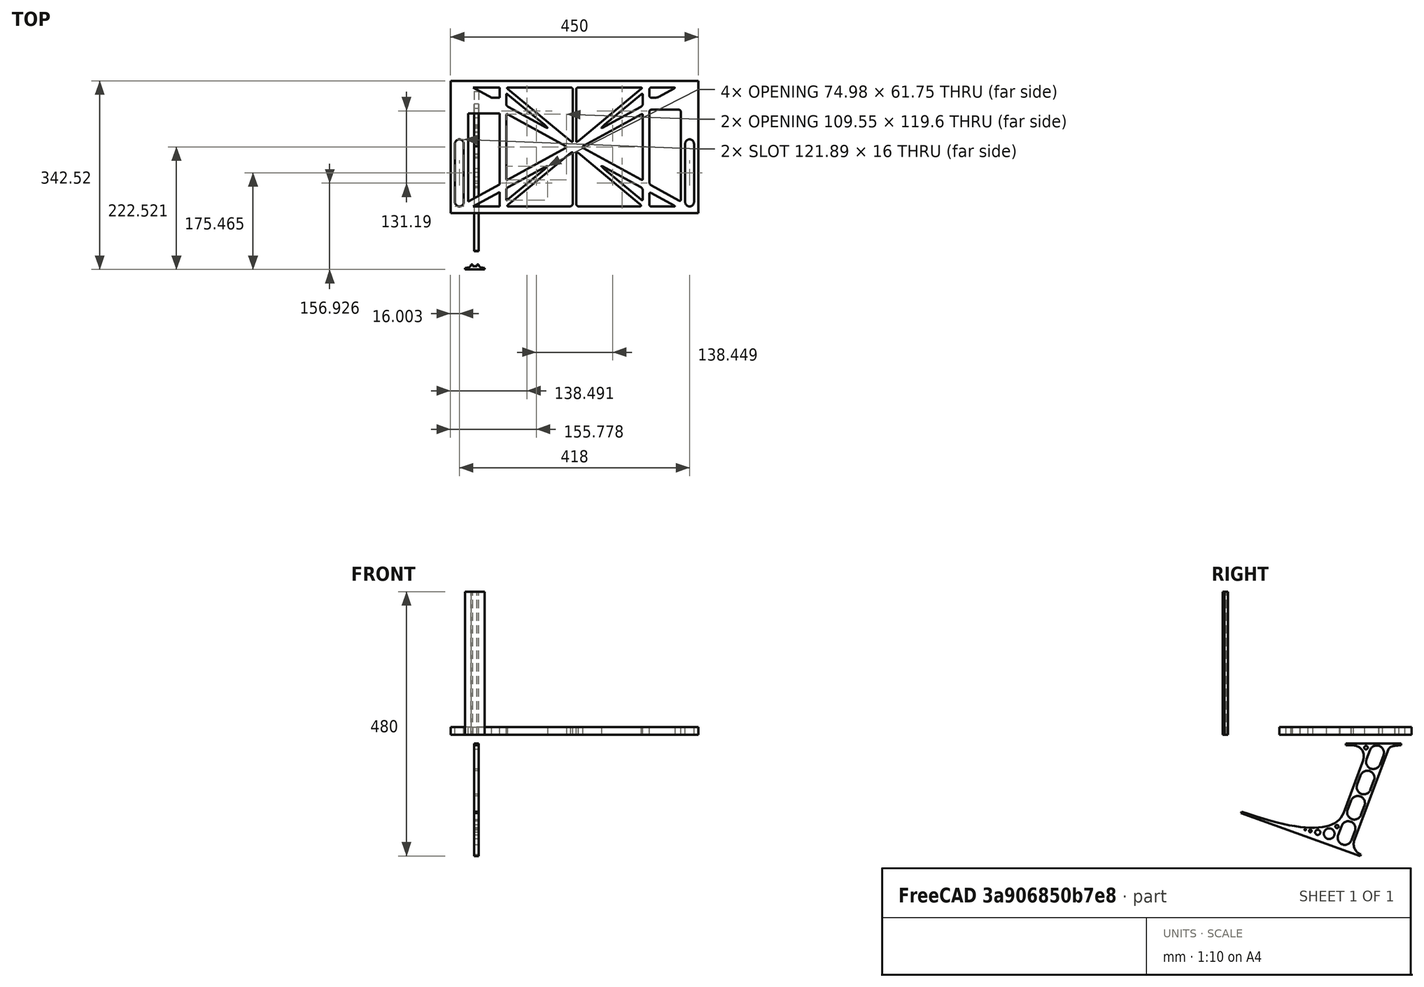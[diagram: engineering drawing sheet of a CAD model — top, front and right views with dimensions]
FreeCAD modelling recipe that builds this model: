
FCSTD DOCUMENT  (FreeCAD 0.19R0.19.2)
Label: laptopStand1156FCStd
License: All rights reserved
LicenseURL: http://en.wikipedia.org/wiki/All_rights_reserved
objects: Sketcher::SketchObject×3, Part::Extrusion×3
note: 6 computed .brp shape members not serialized (recipe doc carries the construction recipe); baked Part::Feature solids carry a one-line shape summary decoded from their .brp

FEATURE [Sketcher::SketchObject] Sketch
  FullyConstrained = true
  sketch-geometry (318):
    g0: LineSegment StartX=-10.9272 StartY=-82.7794 StartZ=0 EndX=46.0728 EndY=-51.4823 EndZ=0
    g1: LineSegment StartX=-10.9272 StartY=77.3346 StartZ=0 EndX=-10.9272 EndY=-82.7794 EndZ=0
    g2: LineSegment StartX=-1.92719 StartY=-91.7794 StartZ=0 EndX=46.0728 EndY=-91.7794 EndZ=0
    g3: LineSegment StartX=46.0728 StartY=-65.424 StartZ=0 EndX=-1.92719 EndY=-91.7794 EndZ=0
    g4: LineSegment StartX=46.0728 StartY=-65.424 StartZ=0 EndX=46.0728 EndY=-91.7794 EndZ=0
    g5: LineSegment StartX=46.0728 StartY=77.3346 StartZ=0 EndX=46.0728 EndY=-51.4823 EndZ=0
    g6: LineSegment StartX=-42.9272 StartY=136.221 StartZ=0 EndX=-42.9272 EndY=-103.779 EndZ=0
    g7: LineSegment StartX=407.073 StartY=136.221 StartZ=0 EndX=407.073 EndY=-103.779 EndZ=0
    g8: ArcOfCircle CenterX=-26.9272 CenterY=22.1087 CenterZ=0 NormalX=0 NormalY=0 NormalZ=1 AngleXU=0 Radius=8 StartAngle=1e-16 EndAngle=3.14159
    g9: ArcOfCircle CenterX=-26.9272 CenterY=-83.7794 CenterZ=0 NormalX=0 NormalY=0 NormalZ=1 AngleXU=0 Radius=8 StartAngle=3.14159 EndAngle=6.28319
    g10: LineSegment StartX=-34.9272 StartY=22.1087 StartZ=0 EndX=-34.9272 EndY=-83.7794 EndZ=0
    g11: LineSegment StartX=-18.9272 StartY=22.1087 StartZ=0 EndX=-18.9272 EndY=-83.7794 EndZ=0
    g12: ArcOfCircle CenterX=391.073 CenterY=22.1087 CenterZ=0 NormalX=0 NormalY=0 NormalZ=1 AngleXU=0 Radius=8 StartAngle=-4.4e-15 EndAngle=3.14159
    g13: LineSegment StartX=399.073 StartY=22.1087 StartZ=0 EndX=399.073 EndY=-83.7794 EndZ=0
    g14: LineSegment StartX=383.073 StartY=22.1087 StartZ=0 EndX=383.073 EndY=-83.7794 EndZ=0
    g15: ArcOfCircle CenterX=391.073 CenterY=-83.7794 CenterZ=0 NormalX=0 NormalY=0 NormalZ=1 AngleXU=0 Radius=8 StartAngle=3.14159 EndAngle=6.28319
    g16: Circle CenterX=175.022 CenterY=27.0628 CenterZ=0 NormalX=0 NormalY=0 NormalZ=1 AngleXU=0 Radius=1
    g17: Circle CenterX=179.022 CenterY=24.8665 CenterZ=0 NormalX=0 NormalY=0 NormalZ=1 AngleXU=0 Radius=1
    g18: Circle CenterX=179.022 CenterY=27.0628 CenterZ=0 NormalX=0 NormalY=0 NormalZ=1 AngleXU=0 Radius=1
    g19: BSplineCurve PolesCount=3 KnotsCount=2 Degree=2 IsPeriodic=0
    g20: GeomPoint X=175.022 Y=27.0628 Z=0
    g21: GeomPoint X=179.022 Y=27.0628 Z=0
    g22: Circle CenterX=189.124 CenterY=27.0628 CenterZ=0 NormalX=0 NormalY=0 NormalZ=1 AngleXU=0 Radius=1
    g23: Circle CenterX=185.124 CenterY=24.8665 CenterZ=0 NormalX=0 NormalY=0 NormalZ=1 AngleXU=0 Radius=1
    g24: Circle CenterX=185.124 CenterY=27.0628 CenterZ=0 NormalX=0 NormalY=0 NormalZ=1 AngleXU=0 Radius=1
    g25: BSplineCurve PolesCount=3 KnotsCount=2 Degree=2 IsPeriodic=0
    g26: GeomPoint X=189.124 Y=27.0628 Z=0
    g27: GeomPoint X=185.124 Y=27.0628 Z=0
    g28: Circle CenterX=175.022 CenterY=5.37834 CenterZ=0 NormalX=0 NormalY=0 NormalZ=1 AngleXU=0 Radius=1
    g29: Circle CenterX=179.022 CenterY=7.57463 CenterZ=0 NormalX=0 NormalY=0 NormalZ=1 AngleXU=0 Radius=1
    g30: Circle CenterX=179.022 CenterY=5.34704 CenterZ=0 NormalX=0 NormalY=0 NormalZ=1 AngleXU=0 Radius=1
    g31: BSplineCurve PolesCount=3 KnotsCount=2 Degree=2 IsPeriodic=0
    g32: GeomPoint X=175.022 Y=5.37834 Z=0
    g33: GeomPoint X=179.022 Y=5.34704 Z=0
    g34: Circle CenterX=189.124 CenterY=5.37834 CenterZ=0 NormalX=0 NormalY=0 NormalZ=1 AngleXU=0 Radius=1
    g35: Circle CenterX=185.124 CenterY=7.57463 CenterZ=0 NormalX=0 NormalY=0 NormalZ=1 AngleXU=0 Radius=1
    g36: Circle CenterX=185.124 CenterY=5.34704 CenterZ=0 NormalX=0 NormalY=0 NormalZ=1 AngleXU=0 Radius=1
    g37: BSplineCurve PolesCount=3 KnotsCount=2 Degree=2 IsPeriodic=0
    g38: GeomPoint X=189.124 Y=5.37834 Z=0
    g39: GeomPoint X=185.124 Y=5.34704 Z=0
    g40: Circle CenterX=165.871 CenterY=18.1458 CenterZ=0 NormalX=0 NormalY=0 NormalZ=1 AngleXU=0 Radius=1
    g41: Circle CenterX=169.377 CenterY=16.2206 CenterZ=0 NormalX=0 NormalY=0 NormalZ=1 AngleXU=0 Radius=1
    g42: Circle CenterX=165.871 CenterY=14.2954 CenterZ=0 NormalX=0 NormalY=0 NormalZ=1 AngleXU=0 Radius=1
    g43: BSplineCurve PolesCount=3 KnotsCount=2 Degree=2 IsPeriodic=0
    g44: GeomPoint X=165.871 Y=18.1458 Z=0
    g45: GeomPoint X=165.871 Y=14.2954 Z=0
    g46: Circle CenterX=198.275 CenterY=18.1458 CenterZ=0 NormalX=0 NormalY=0 NormalZ=1 AngleXU=0 Radius=1
    g47: Circle CenterX=194.768 CenterY=16.2206 CenterZ=0 NormalX=0 NormalY=0 NormalZ=1 AngleXU=0 Radius=1
    g48: Circle CenterX=198.275 CenterY=14.2954 CenterZ=0 NormalX=0 NormalY=0 NormalZ=1 AngleXU=0 Radius=1
    g49: BSplineCurve PolesCount=3 KnotsCount=2 Degree=2 IsPeriodic=0
    g50: GeomPoint X=198.275 Y=18.1458 Z=0
    g51: GeomPoint X=198.275 Y=14.2954 Z=0
    g52: LineSegment StartX=407.073 StartY=-103.779 StartZ=0 EndX=-42.9272 EndY=-103.779 EndZ=0
    g53: LineSegment StartX=407.073 StartY=136.221 StartZ=0 EndX=-42.9272 EndY=136.221 EndZ=0
    g54: LineSegment StartX=46.0728 StartY=77.3346 StartZ=0 EndX=-10.9272 EndY=77.3346 EndZ=0
    g55: LineSegment StartX=46.0728 StartY=105.865 StartZ=0 EndX=31.5028 EndY=105.865 EndZ=0
    g56: LineSegment StartX=46.0728 StartY=124.221 StartZ=0 EndX=46.0728 EndY=105.865 EndZ=0
    g57: LineSegment StartX=-1.92719 StartY=124.221 StartZ=0 EndX=31.5028 EndY=105.865 EndZ=0
    g58: LineSegment StartX=46.0728 StartY=124.221 StartZ=0 EndX=-1.92719 EndY=124.221 EndZ=0
    g59: Circle CenterX=125.607 CenterY=54.1951 CenterZ=0 NormalX=0 NormalY=0 NormalZ=1 AngleXU=0 Radius=1
    g60: Circle CenterX=139.632 CenterY=46.4944 CenterZ=0 NormalX=0 NormalY=0 NormalZ=1 AngleXU=0 Radius=1
    g61: Circle CenterX=127.326 CenterY=56.7187 CenterZ=0 NormalX=0 NormalY=0 NormalZ=1 AngleXU=0 Radius=1
    g62: BSplineCurve PolesCount=3 KnotsCount=2 Degree=2 IsPeriodic=0
    g63: GeomPoint X=125.607 Y=54.1951 Z=0
    g64: GeomPoint X=127.326 Y=56.7187 Z=0
    g65: Circle CenterX=236.821 CenterY=56.7187 CenterZ=0 NormalX=0 NormalY=0 NormalZ=1 AngleXU=0 Radius=1
    g66: Circle CenterX=224.513 CenterY=46.4944 CenterZ=0 NormalX=0 NormalY=0 NormalZ=1 AngleXU=0 Radius=1
    g67: Circle CenterX=238.538 CenterY=54.1951 CenterZ=0 NormalX=0 NormalY=0 NormalZ=1 AngleXU=0 Radius=1
    g68: BSplineCurve PolesCount=3 KnotsCount=2 Degree=2 IsPeriodic=0
    g69: GeomPoint X=236.821 Y=56.7187 Z=0
    g70: GeomPoint X=238.538 Y=54.1951 Z=0
    g71: Circle CenterX=238.538 CenterY=-21.7539 CenterZ=0 NormalX=0 NormalY=0 NormalZ=1 AngleXU=0 Radius=1
    g72: Circle CenterX=224.513 CenterY=-14.0532 CenterZ=0 NormalX=0 NormalY=0 NormalZ=1 AngleXU=0 Radius=1
    g73: Circle CenterX=236.821 CenterY=-24.2775 CenterZ=0 NormalX=0 NormalY=0 NormalZ=1 AngleXU=0 Radius=1
    g74: BSplineCurve PolesCount=3 KnotsCount=2 Degree=2 IsPeriodic=0
    g75: GeomPoint X=238.538 Y=-21.7539 Z=0
    g76: GeomPoint X=236.821 Y=-24.2775 Z=0
    g77: Circle CenterX=125.607 CenterY=-21.7539 CenterZ=0 NormalX=0 NormalY=0 NormalZ=1 AngleXU=0 Radius=1
    g78: Circle CenterX=139.632 CenterY=-14.0532 CenterZ=0 NormalX=0 NormalY=0 NormalZ=1 AngleXU=0 Radius=1
    g79: Circle CenterX=127.325 CenterY=-24.2775 CenterZ=0 NormalX=0 NormalY=0 NormalZ=1 AngleXU=0 Radius=1
    g80: BSplineCurve PolesCount=3 KnotsCount=2 Degree=2 IsPeriodic=0
    g81: GeomPoint X=125.607 Y=-21.7539 Z=0
    g82: GeomPoint X=127.325 Y=-24.2775 Z=0
    g83: Circle CenterX=302.996 CenterY=111.695 CenterZ=0 NormalX=0 NormalY=0 NormalZ=1 AngleXU=0 Radius=1
    g84: Circle CenterX=306.073 CenterY=114.251 CenterZ=0 NormalX=0 NormalY=0 NormalZ=1 AngleXU=0 Radius=1
    g85: Circle CenterX=306.073 CenterY=110.251 CenterZ=0 NormalX=0 NormalY=0 NormalZ=1 AngleXU=0 Radius=1
    g86: BSplineCurve PolesCount=3 KnotsCount=2 Degree=2 IsPeriodic=0
    g87: GeomPoint X=302.996 Y=111.695 Z=0
    g88: GeomPoint X=306.073 Y=110.251 Z=0
    g89: Circle CenterX=306.073 CenterY=95.2763 CenterZ=0 NormalX=0 NormalY=0 NormalZ=1 AngleXU=0 Radius=1
    g90: Circle CenterX=306.073 CenterY=91.2763 CenterZ=0 NormalX=0 NormalY=0 NormalZ=1 AngleXU=0 Radius=1
    g91: Circle CenterX=302.567 CenterY=89.3511 CenterZ=0 NormalX=0 NormalY=0 NormalZ=1 AngleXU=0 Radius=1
    g92: BSplineCurve PolesCount=3 KnotsCount=2 Degree=2 IsPeriodic=0
    g93: GeomPoint X=306.073 Y=95.2763 Z=0
    g94: GeomPoint X=302.567 Y=89.3511 Z=0
    g95: LineSegment StartX=306.073 StartY=110.251 StartZ=0 EndX=306.073 EndY=95.2763 EndZ=0
    g96: LineSegment StartX=302.996 StartY=111.695 StartZ=0 EndX=236.821 EndY=56.7187 EndZ=0
    g97: LineSegment StartX=238.538 StartY=54.1951 StartZ=0 EndX=302.567 EndY=89.3511 EndZ=0
    g98: Circle CenterX=61.1496 CenterY=111.695 CenterZ=0 NormalX=0 NormalY=0 NormalZ=1 AngleXU=0 Radius=1
    g99: Circle CenterX=58.0728 CenterY=114.251 CenterZ=0 NormalX=0 NormalY=0 NormalZ=1 AngleXU=0 Radius=1
    g100: Circle CenterX=58.0728 CenterY=110.251 CenterZ=0 NormalX=0 NormalY=0 NormalZ=1 AngleXU=0 Radius=1
    g101: BSplineCurve PolesCount=3 KnotsCount=2 Degree=2 IsPeriodic=0
    g102: GeomPoint X=61.1496 Y=111.695 Z=0
    g103: GeomPoint X=58.0728 Y=110.251 Z=0
    g104: Circle CenterX=61.5791 CenterY=89.3511 CenterZ=0 NormalX=0 NormalY=0 NormalZ=1 AngleXU=0 Radius=1
    g105: Circle CenterX=58.0728 CenterY=91.2763 CenterZ=0 NormalX=0 NormalY=0 NormalZ=1 AngleXU=0 Radius=1
    g106: Circle CenterX=58.0728 CenterY=95.2763 CenterZ=0 NormalX=0 NormalY=0 NormalZ=1 AngleXU=0 Radius=1
    g107: BSplineCurve PolesCount=3 KnotsCount=2 Degree=2 IsPeriodic=0
    g108: GeomPoint X=61.5791 Y=89.3511 Z=0
    g109: GeomPoint X=58.0728 Y=95.2763 Z=0
    g110: LineSegment StartX=58.0728 StartY=110.251 StartZ=0 EndX=58.0728 EndY=95.2763 EndZ=0
    g111: LineSegment StartX=61.1496 StartY=111.695 StartZ=0 EndX=127.326 EndY=56.7187 EndZ=0
    g112: LineSegment StartX=125.607 StartY=54.1951 StartZ=0 EndX=61.5791 EndY=89.3511 EndZ=0
    g113: Circle CenterX=61.5791 CenterY=-56.9099 CenterZ=0 NormalX=0 NormalY=0 NormalZ=1 AngleXU=0 Radius=1
    g114: Circle CenterX=58.0728 CenterY=-58.8351 CenterZ=0 NormalX=0 NormalY=0 NormalZ=1 AngleXU=0 Radius=1
    g115: Circle CenterX=58.0728 CenterY=-62.8351 CenterZ=0 NormalX=0 NormalY=0 NormalZ=1 AngleXU=0 Radius=1
    g116: BSplineCurve PolesCount=3 KnotsCount=2 Degree=2 IsPeriodic=0
    g117: GeomPoint X=61.5791 Y=-56.9099 Z=0
    g118: GeomPoint X=58.0728 Y=-62.8351 Z=0
    g119: Circle CenterX=58.0728 CenterY=-77.8102 CenterZ=0 NormalX=0 NormalY=0 NormalZ=1 AngleXU=0 Radius=1
    g120: Circle CenterX=58.0728 CenterY=-81.8102 CenterZ=0 NormalX=0 NormalY=0 NormalZ=1 AngleXU=0 Radius=1
    g121: Circle CenterX=61.1496 CenterY=-79.2541 CenterZ=0 NormalX=0 NormalY=0 NormalZ=1 AngleXU=0 Radius=1
    g122: BSplineCurve PolesCount=3 KnotsCount=2 Degree=2 IsPeriodic=0
    g123: GeomPoint X=58.0728 Y=-77.8102 Z=0
    g124: GeomPoint X=61.1496 Y=-79.2541 Z=0
    g125: LineSegment StartX=58.0728 StartY=-62.8351 StartZ=0 EndX=58.0728 EndY=-77.8102 EndZ=0
    g126: LineSegment StartX=61.1496 StartY=-79.2541 StartZ=0 EndX=127.325 EndY=-24.2775 EndZ=0
    g127: LineSegment StartX=125.607 StartY=-21.7539 StartZ=0 EndX=61.5791 EndY=-56.9099 EndZ=0
    g128: Circle CenterX=302.567 CenterY=-56.9099 CenterZ=0 NormalX=0 NormalY=0 NormalZ=1 AngleXU=0 Radius=1
    g129: Circle CenterX=306.073 CenterY=-58.8351 CenterZ=0 NormalX=0 NormalY=0 NormalZ=1 AngleXU=0 Radius=1
    g130: Circle CenterX=306.073 CenterY=-62.8351 CenterZ=0 NormalX=0 NormalY=0 NormalZ=1 AngleXU=0 Radius=1
    g131: BSplineCurve PolesCount=3 KnotsCount=2 Degree=2 IsPeriodic=0
    g132: GeomPoint X=302.567 Y=-56.9099 Z=0
    g133: GeomPoint X=306.073 Y=-62.8351 Z=0
    g134: Circle CenterX=302.996 CenterY=-79.2541 CenterZ=0 NormalX=0 NormalY=0 NormalZ=1 AngleXU=0 Radius=1
    g135: Circle CenterX=306.073 CenterY=-81.8102 CenterZ=0 NormalX=0 NormalY=0 NormalZ=1 AngleXU=0 Radius=1
    g136: Circle CenterX=306.073 CenterY=-77.8102 CenterZ=0 NormalX=0 NormalY=0 NormalZ=1 AngleXU=0 Radius=1
    g137: BSplineCurve PolesCount=3 KnotsCount=2 Degree=2 IsPeriodic=0
    g138: GeomPoint X=302.996 Y=-79.2541 Z=0
    g139: GeomPoint X=306.073 Y=-77.8102 Z=0
    g140: LineSegment StartX=306.073 StartY=-62.8351 StartZ=0 EndX=306.073 EndY=-77.8102 EndZ=0
    g141: LineSegment StartX=302.996 StartY=-79.2541 StartZ=0 EndX=236.821 EndY=-24.2775 EndZ=0
    g142: LineSegment StartX=238.538 StartY=-21.7539 StartZ=0 EndX=302.567 EndY=-56.9099 EndZ=0
    g143: Circle CenterX=61.6457 CenterY=-88.8112 CenterZ=0 NormalX=0 NormalY=0 NormalZ=1 AngleXU=0 Radius=1
    g144: Circle CenterX=58.0728 CenterY=-91.7794 CenterZ=0 NormalX=0 NormalY=0 NormalZ=1 AngleXU=0 Radius=1
    g145: Circle CenterX=63.9135 CenterY=-91.7794 CenterZ=0 NormalX=0 NormalY=0 NormalZ=1 AngleXU=0 Radius=1
    g146: BSplineCurve PolesCount=3 KnotsCount=2 Degree=2 IsPeriodic=0
    g147: GeomPoint X=61.6457 Y=-88.8112 Z=0
    g148: GeomPoint X=63.9135 Y=-91.7794 Z=0
    g149: Circle CenterX=179.022 CenterY=-85.8163 CenterZ=0 NormalX=0 NormalY=0 NormalZ=1 AngleXU=0 Radius=1
    g150: Circle CenterX=179.022 CenterY=-91.7794 CenterZ=0 NormalX=0 NormalY=0 NormalZ=1 AngleXU=0 Radius=1
    g151: Circle CenterX=171.895 CenterY=-91.7794 CenterZ=0 NormalX=0 NormalY=0 NormalZ=1 AngleXU=0 Radius=1
    g152: BSplineCurve PolesCount=3 KnotsCount=2 Degree=2 IsPeriodic=0
    g153: GeomPoint X=179.022 Y=-85.8163 Z=0
    g154: GeomPoint X=171.895 Y=-91.7794 Z=0
    g155: Circle CenterX=185.124 CenterY=-86.2028 CenterZ=0 NormalX=0 NormalY=0 NormalZ=1 AngleXU=0 Radius=1
    g156: Circle CenterX=185.124 CenterY=-91.7794 CenterZ=0 NormalX=0 NormalY=0 NormalZ=1 AngleXU=0 Radius=1
    g157: Circle CenterX=191.747 CenterY=-91.7794 CenterZ=0 NormalX=0 NormalY=0 NormalZ=1 AngleXU=0 Radius=1
    g158: BSplineCurve PolesCount=3 KnotsCount=2 Degree=2 IsPeriodic=0
    g159: GeomPoint X=185.124 Y=-86.2028 Z=0
    g160: GeomPoint X=191.747 Y=-91.7794 Z=0
    g161: Circle CenterX=299.888 CenterY=-86.6413 CenterZ=0 NormalX=0 NormalY=0 NormalZ=1 AngleXU=0 Radius=1
    g162: Circle CenterX=306.073 CenterY=-91.7794 CenterZ=0 NormalX=0 NormalY=0 NormalZ=1 AngleXU=0 Radius=1
    g163: Circle CenterX=298.776 CenterY=-91.7794 CenterZ=0 NormalX=0 NormalY=0 NormalZ=1 AngleXU=0 Radius=1
    g164: BSplineCurve PolesCount=3 KnotsCount=2 Degree=2 IsPeriodic=0
    g165: GeomPoint X=299.888 Y=-86.6413 Z=0
    g166: GeomPoint X=298.776 Y=-91.7794 Z=0
    g167: LineSegment StartX=189.124 StartY=5.37834 StartZ=0 EndX=299.888 EndY=-86.6413 EndZ=0
    g168: LineSegment StartX=298.776 StartY=-91.7794 StartZ=0 EndX=191.747 EndY=-91.7794 EndZ=0
    g169: LineSegment StartX=185.124 StartY=-86.2028 StartZ=0 EndX=185.124 EndY=5.34704 EndZ=0
    g170: LineSegment StartX=179.022 StartY=5.34704 StartZ=0 EndX=179.022 EndY=-85.8163 EndZ=0
    g171: LineSegment StartX=171.895 StartY=-91.7794 StartZ=0 EndX=63.9135 EndY=-91.7794 EndZ=0
    g172: LineSegment StartX=61.6457 StartY=-88.8112 StartZ=0 EndX=175.022 EndY=5.37834 EndZ=0
    g173: Circle CenterX=302.073 CenterY=124.221 CenterZ=0 NormalX=0 NormalY=0 NormalZ=1 AngleXU=0 Radius=1
    g174: Circle CenterX=306.073 CenterY=124.221 CenterZ=0 NormalX=0 NormalY=0 NormalZ=1 AngleXU=0 Radius=1
    g175: Circle CenterX=302.996 CenterY=121.665 CenterZ=0 NormalX=0 NormalY=0 NormalZ=1 AngleXU=0 Radius=1
    g176: BSplineCurve PolesCount=3 KnotsCount=2 Degree=2 IsPeriodic=0
    g177: GeomPoint X=302.073 Y=124.221 Z=0
    g178: GeomPoint X=302.996 Y=121.665 Z=0
    g179: Circle CenterX=189.124 CenterY=124.221 CenterZ=0 NormalX=0 NormalY=0 NormalZ=1 AngleXU=0 Radius=1
    g180: Circle CenterX=185.124 CenterY=124.221 CenterZ=0 NormalX=0 NormalY=0 NormalZ=1 AngleXU=0 Radius=1
    g181: Circle CenterX=185.124 CenterY=120.221 CenterZ=0 NormalX=0 NormalY=0 NormalZ=1 AngleXU=0 Radius=1
    g182: BSplineCurve PolesCount=3 KnotsCount=2 Degree=2 IsPeriodic=0
    g183: GeomPoint X=189.124 Y=124.221 Z=0
    g184: GeomPoint X=185.124 Y=120.221 Z=0
    g185: Circle CenterX=175.022 CenterY=124.221 CenterZ=0 NormalX=0 NormalY=0 NormalZ=1 AngleXU=0 Radius=1
    g186: Circle CenterX=179.022 CenterY=124.221 CenterZ=0 NormalX=0 NormalY=0 NormalZ=1 AngleXU=0 Radius=1
    g187: Circle CenterX=179.022 CenterY=120.221 CenterZ=0 NormalX=0 NormalY=0 NormalZ=1 AngleXU=0 Radius=1
    g188: BSplineCurve PolesCount=3 KnotsCount=2 Degree=2 IsPeriodic=0
    g189: GeomPoint X=175.022 Y=124.221 Z=0
    g190: GeomPoint X=179.022 Y=120.221 Z=0
    g191: Circle CenterX=62.0728 CenterY=124.221 CenterZ=0 NormalX=0 NormalY=0 NormalZ=1 AngleXU=0 Radius=1
    g192: Circle CenterX=58.0728 CenterY=124.221 CenterZ=0 NormalX=0 NormalY=0 NormalZ=1 AngleXU=0 Radius=1
    g193: Circle CenterX=61.1496 CenterY=121.665 CenterZ=0 NormalX=0 NormalY=0 NormalZ=1 AngleXU=0 Radius=1
    g194: BSplineCurve PolesCount=3 KnotsCount=2 Degree=2 IsPeriodic=0
    g195: GeomPoint X=62.0728 Y=124.221 Z=0
    g196: GeomPoint X=61.1496 Y=121.665 Z=0
    g197: LineSegment StartX=62.0728 StartY=124.221 StartZ=0 EndX=175.022 EndY=124.221 EndZ=0
    g198: LineSegment StartX=179.022 StartY=120.221 StartZ=0 EndX=179.022 EndY=27.0628 EndZ=0
    g199: LineSegment StartX=185.124 StartY=27.0628 StartZ=0 EndX=185.124 EndY=120.221 EndZ=0
    g200: LineSegment StartX=189.124 StartY=124.221 StartZ=0 EndX=302.073 EndY=124.221 EndZ=0
    g201: LineSegment StartX=302.996 StartY=121.665 StartZ=0 EndX=189.124 EndY=27.0628 EndZ=0
    g202: LineSegment StartX=175.022 StartY=27.0628 StartZ=0 EndX=61.1496 EndY=121.665 EndZ=0
    g203: Circle CenterX=61.5791 CenterY=75.4095 CenterZ=0 NormalX=0 NormalY=0 NormalZ=1 AngleXU=0 Radius=1
    g204: Circle CenterX=58.0728 CenterY=77.3346 CenterZ=0 NormalX=0 NormalY=0 NormalZ=1 AngleXU=0 Radius=1
    g205: Circle CenterX=58.0728 CenterY=73.3346 CenterZ=0 NormalX=0 NormalY=0 NormalZ=1 AngleXU=0 Radius=1
    g206: BSplineCurve PolesCount=3 KnotsCount=2 Degree=2 IsPeriodic=0
    g207: GeomPoint X=61.5791 Y=75.4095 Z=0
    g208: GeomPoint X=58.0728 Y=73.3346 Z=0
    g209: Circle CenterX=58.0728 CenterY=-40.8935 CenterZ=0 NormalX=0 NormalY=0 NormalZ=1 AngleXU=0 Radius=1
    g210: Circle CenterX=58.0728 CenterY=-44.8935 CenterZ=0 NormalX=0 NormalY=0 NormalZ=1 AngleXU=0 Radius=1
    g211: Circle CenterX=61.5791 CenterY=-42.9683 CenterZ=0 NormalX=0 NormalY=0 NormalZ=1 AngleXU=0 Radius=1
    g212: BSplineCurve PolesCount=3 KnotsCount=2 Degree=2 IsPeriodic=0
    g213: GeomPoint X=58.0728 Y=-40.8935 Z=0
    g214: GeomPoint X=61.5791 Y=-42.9683 Z=0
    g215: LineSegment StartX=61.5791 StartY=-42.9683 StartZ=0 EndX=165.871 EndY=14.2954 EndZ=0
    g216: LineSegment StartX=165.871 StartY=18.1458 StartZ=0 EndX=61.5791 EndY=75.4095 EndZ=0
    g217: LineSegment StartX=58.0728 StartY=73.3346 StartZ=0 EndX=58.0728 EndY=-40.8935 EndZ=0
    g218: Circle CenterX=302.567 CenterY=-42.9683 CenterZ=0 NormalX=0 NormalY=0 NormalZ=1 AngleXU=0 Radius=1
    g219: Circle CenterX=306.073 CenterY=-44.8935 CenterZ=0 NormalX=0 NormalY=0 NormalZ=1 AngleXU=0 Radius=1
    g220: Circle CenterX=306.073 CenterY=-40.8935 CenterZ=0 NormalX=0 NormalY=0 NormalZ=1 AngleXU=0 Radius=1
    g221: BSplineCurve PolesCount=3 KnotsCount=2 Degree=2 IsPeriodic=0
    g222: GeomPoint X=302.567 Y=-42.9683 Z=0
    g223: GeomPoint X=306.073 Y=-40.8935 Z=0
    g224: Circle CenterX=306.073 CenterY=73.3346 CenterZ=0 NormalX=0 NormalY=0 NormalZ=1 AngleXU=0 Radius=1
    g225: Circle CenterX=306.073 CenterY=77.3346 CenterZ=0 NormalX=0 NormalY=0 NormalZ=1 AngleXU=0 Radius=1
    g226: Circle CenterX=302.567 CenterY=75.4095 CenterZ=0 NormalX=0 NormalY=0 NormalZ=1 AngleXU=0 Radius=1
    g227: BSplineCurve PolesCount=3 KnotsCount=2 Degree=2 IsPeriodic=0
    g228: GeomPoint X=306.073 Y=73.3346 Z=0
    g229: GeomPoint X=302.567 Y=75.4095 Z=0
    g230: LineSegment StartX=302.567 StartY=-42.9683 StartZ=0 EndX=198.275 EndY=14.2954 EndZ=0
    g231: LineSegment StartX=198.275 StartY=18.1458 StartZ=0 EndX=302.567 EndY=75.4095 EndZ=0
    g232: LineSegment StartX=306.073 StartY=73.3346 StartZ=0 EndX=306.073 EndY=-40.8935 EndZ=0
    g233: LineSegment StartX=322.073 StartY=105.865 StartZ=0 EndX=328.643 EndY=105.865 EndZ=0
    g234: LineSegment StartX=318.073 StartY=120.221 StartZ=0 EndX=318.073 EndY=109.865 EndZ=0
    g235: LineSegment StartX=336.157 StartY=107.779 StartZ=0 EndX=362.567 EndY=122.294 EndZ=0
    g236: Circle CenterX=362.073 CenterY=124.221 CenterZ=0 NormalX=0 NormalY=0 NormalZ=1 AngleXU=0 Radius=1
    g237: Circle CenterX=366.073 CenterY=124.221 CenterZ=0 NormalX=0 NormalY=0 NormalZ=1 AngleXU=0 Radius=1
    g238: Circle CenterX=362.567 CenterY=122.294 CenterZ=0 NormalX=0 NormalY=0 NormalZ=1 AngleXU=0 Radius=1
    g239: BSplineCurve PolesCount=3 KnotsCount=2 Degree=2 IsPeriodic=0
    g240: GeomPoint X=362.073 Y=124.221 Z=0
    g241: GeomPoint X=362.567 Y=122.294 Z=0
    g242: Circle CenterX=322.073 CenterY=124.221 CenterZ=0 NormalX=0 NormalY=0 NormalZ=1 AngleXU=0 Radius=1
    g243: Circle CenterX=318.073 CenterY=124.221 CenterZ=0 NormalX=0 NormalY=0 NormalZ=1 AngleXU=0 Radius=1
    g244: Circle CenterX=318.073 CenterY=120.221 CenterZ=0 NormalX=0 NormalY=0 NormalZ=1 AngleXU=0 Radius=1
    g245: BSplineCurve PolesCount=3 KnotsCount=2 Degree=2 IsPeriodic=0
    g246: GeomPoint X=322.073 Y=124.221 Z=0
    g247: GeomPoint X=318.073 Y=120.221 Z=0
    g248: Circle CenterX=322.073 CenterY=105.865 CenterZ=0 NormalX=0 NormalY=0 NormalZ=1 AngleXU=0 Radius=1
    g249: Circle CenterX=318.073 CenterY=105.865 CenterZ=0 NormalX=0 NormalY=0 NormalZ=1 AngleXU=0 Radius=1
    g250: Circle CenterX=318.073 CenterY=109.865 CenterZ=0 NormalX=0 NormalY=0 NormalZ=1 AngleXU=0 Radius=1
    g251: BSplineCurve PolesCount=3 KnotsCount=2 Degree=2 IsPeriodic=0
    g252: GeomPoint X=322.073 Y=105.865 Z=0
    g253: GeomPoint X=318.073 Y=109.865 Z=0
    g254: Circle CenterX=336.157 CenterY=107.779 CenterZ=0 NormalX=0 NormalY=0 NormalZ=1 AngleXU=0 Radius=1
    g255: Circle CenterX=332.651 CenterY=105.853 CenterZ=0 NormalX=0 NormalY=0 NormalZ=1 AngleXU=0 Radius=1
    g256: Circle CenterX=328.643 CenterY=105.865 CenterZ=0 NormalX=0 NormalY=0 NormalZ=1 AngleXU=0 Radius=1
    g257: BSplineCurve PolesCount=3 KnotsCount=2 Degree=2 IsPeriodic=0
    g258: GeomPoint X=336.157 Y=107.779 Z=0
    g259: GeomPoint X=328.643 Y=105.865 Z=0
    g260: LineSegment StartX=322.073 StartY=124.221 StartZ=0 EndX=362.073 EndY=124.221 EndZ=0
    g261: Circle CenterX=371.567 CenterY=-80.8644 CenterZ=0 NormalX=0 NormalY=0 NormalZ=1 AngleXU=0 Radius=1
    g262: Circle CenterX=375.073 CenterY=-82.7896 CenterZ=0 NormalX=0 NormalY=0 NormalZ=1 AngleXU=0 Radius=1
    g263: Circle CenterX=375.073 CenterY=-78.7896 CenterZ=0 NormalX=0 NormalY=0 NormalZ=1 AngleXU=0 Radius=1
    g264: BSplineCurve PolesCount=3 KnotsCount=2 Degree=2 IsPeriodic=0
    g265: GeomPoint X=371.567 Y=-80.8644 Z=0
    g266: GeomPoint X=375.073 Y=-78.7896 Z=0
    g267: Circle CenterX=321.579 CenterY=-53.4075 CenterZ=0 NormalX=0 NormalY=0 NormalZ=1 AngleXU=0 Radius=1
    g268: Circle CenterX=318.073 CenterY=-51.4823 CenterZ=0 NormalX=0 NormalY=0 NormalZ=1 AngleXU=0 Radius=1
    g269: Circle CenterX=318.073 CenterY=-47.4823 CenterZ=0 NormalX=0 NormalY=0 NormalZ=1 AngleXU=0 Radius=1
    g270: BSplineCurve PolesCount=3 KnotsCount=2 Degree=2 IsPeriodic=0
    g271: GeomPoint X=321.579 Y=-53.4075 Z=0
    g272: GeomPoint X=318.073 Y=-47.4823 Z=0
    g273: Circle CenterX=318.073 CenterY=79.9235 CenterZ=0 NormalX=0 NormalY=0 NormalZ=1 AngleXU=0 Radius=1
    g274: Circle CenterX=318.073 CenterY=83.9235 CenterZ=0 NormalX=0 NormalY=0 NormalZ=1 AngleXU=0 Radius=1
    g275: Circle CenterX=322.073 CenterY=83.9235 CenterZ=0 NormalX=0 NormalY=0 NormalZ=1 AngleXU=0 Radius=1
    g276: BSplineCurve PolesCount=3 KnotsCount=2 Degree=2 IsPeriodic=0
    g277: GeomPoint X=318.073 Y=79.9235 Z=0
    g278: GeomPoint X=322.073 Y=83.9235 Z=0
    g279: Circle CenterX=375.073 CenterY=79.9235 CenterZ=0 NormalX=0 NormalY=0 NormalZ=1 AngleXU=0 Radius=1
    g280: Circle CenterX=375.073 CenterY=83.9235 CenterZ=0 NormalX=0 NormalY=0 NormalZ=1 AngleXU=0 Radius=1
    g281: Circle CenterX=371.073 CenterY=83.9235 CenterZ=0 NormalX=0 NormalY=0 NormalZ=1 AngleXU=0 Radius=1
    g282: BSplineCurve PolesCount=3 KnotsCount=2 Degree=2 IsPeriodic=0
    g283: GeomPoint X=375.073 Y=79.9235 Z=0
    g284: GeomPoint X=371.073 Y=83.9235 Z=0
    g285: LineSegment StartX=322.073 StartY=83.9235 StartZ=0 EndX=371.073 EndY=83.9235 EndZ=0
    g286: LineSegment StartX=375.073 StartY=79.9235 StartZ=0 EndX=375.073 EndY=-78.7896 EndZ=0
    g287: LineSegment StartX=371.567 StartY=-80.8644 StartZ=0 EndX=321.579 EndY=-53.4075 EndZ=0
    g288: LineSegment StartX=318.073 StartY=-47.4823 StartZ=0 EndX=318.073 EndY=79.9235 EndZ=0
    g289: Circle CenterX=321.579 CenterY=-67.3492 CenterZ=0 NormalX=0 NormalY=0 NormalZ=1 AngleXU=0 Radius=1
    g290: Circle CenterX=318.073 CenterY=-65.424 CenterZ=0 NormalX=0 NormalY=0 NormalZ=1 AngleXU=0 Radius=1
    g291: Circle CenterX=318.073 CenterY=-69.424 CenterZ=0 NormalX=0 NormalY=0 NormalZ=1 AngleXU=0 Radius=1
    g292: BSplineCurve PolesCount=3 KnotsCount=2 Degree=2 IsPeriodic=0
    g293: GeomPoint X=321.579 Y=-67.3492 Z=0
    g294: GeomPoint X=318.073 Y=-69.424 Z=0
    g295: Circle CenterX=362.567 CenterY=-89.8542 CenterZ=0 NormalX=0 NormalY=0 NormalZ=1 AngleXU=0 Radius=1
    g296: Circle CenterX=366.073 CenterY=-91.7794 CenterZ=0 NormalX=0 NormalY=0 NormalZ=1 AngleXU=0 Radius=1
    g297: Circle CenterX=362.073 CenterY=-91.7794 CenterZ=0 NormalX=0 NormalY=0 NormalZ=1 AngleXU=0 Radius=1
    g298: BSplineCurve PolesCount=3 KnotsCount=2 Degree=2 IsPeriodic=0
    g299: GeomPoint X=362.567 Y=-89.8542 Z=0
    g300: GeomPoint X=362.073 Y=-91.7794 Z=0
    g301: Circle CenterX=322.073 CenterY=-91.7794 CenterZ=0 NormalX=0 NormalY=0 NormalZ=1 AngleXU=0 Radius=1
    g302: Circle CenterX=318.073 CenterY=-91.7794 CenterZ=0 NormalX=0 NormalY=0 NormalZ=1 AngleXU=0 Radius=1
    g303: Circle CenterX=318.073 CenterY=-87.7794 CenterZ=0 NormalX=0 NormalY=0 NormalZ=1 AngleXU=0 Radius=1
    g304: BSplineCurve PolesCount=3 KnotsCount=2 Degree=2 IsPeriodic=0
    g305: GeomPoint X=322.073 Y=-91.7794 Z=0
    g306: GeomPoint X=318.073 Y=-87.7794 Z=0
    g307: LineSegment StartX=362.567 StartY=-89.8542 StartZ=0 EndX=321.579 EndY=-67.3492 EndZ=0
    g308: LineSegment StartX=318.073 StartY=-69.424 StartZ=0 EndX=318.073 EndY=-87.7794 EndZ=0
    g309: LineSegment StartX=322.073 StartY=-91.7794 StartZ=0 EndX=362.073 EndY=-91.7794 EndZ=0
    g310: LineSegment StartX=-1.92719 StartY=124.221 StartZ=0 EndX=2.07281 EndY=124.221 EndZ=0
    g311: LineSegment StartX=-1.92719 StartY=124.221 StartZ=0 EndX=1.57905 EndY=122.295 EndZ=0
    g312: LineSegment StartX=31.5028 StartY=105.865 StartZ=0 EndX=27.9965 EndY=107.79 EndZ=0
    g313: LineSegment StartX=31.5028 StartY=105.865 StartZ=0 EndX=35.5028 EndY=105.865 EndZ=0
    g314: LineSegment StartX=46.0728 StartY=105.865 StartZ=0 EndX=42.0728 EndY=105.865 EndZ=0
    g315: LineSegment StartX=46.0728 StartY=105.865 StartZ=0 EndX=46.0728 EndY=109.865 EndZ=0
    g316: LineSegment StartX=46.0728 StartY=124.221 StartZ=0 EndX=46.0728 EndY=120.221 EndZ=0
    g317: LineSegment StartX=46.0728 StartY=124.221 StartZ=0 EndX=42.0728 EndY=124.221 EndZ=0
  constraints (543):
    c: Horizontal(g2)
    c: Coincident(g4,g3)
    c: Coincident(g0,g5)
    c: Block(g4)
    c: Block(g3)
    c: Block(g0)
    c: Block(g1)
    c: Block(g2)
    c: Vertical(g6)
    c: Vertical(g7)
    c: Block(g7)
    c: Block(g6)
    c: Tangent(g8,g11) = 1.5708
    c: Tangent(g8,g10) = -1.5708
    c: Tangent(g10,g9) = -1.5708
    c: Tangent(g11,g9) = 1.5708
    c: Vertical(g10)
    c: Equal(g8,g9)
    c: Block(g11)
    c: Block(g10)
    c: Tangent(g12,g13) = 1.5708
    c: Tangent(g13,g15) = 1.5708
    c: Equal(g12,g15)
    c: Coincident(g14,g12)
    c: Coincident(g14,g15)
    c: Block(g13)
    c: Block(g14)
    c: Weight(g16) = 1
    c: Equal(g16,g17)
    c: Equal(g16,g18)
    c: InternalAlignment(g16,g19)
    c: InternalAlignment(g17,g19)
    c: InternalAlignment(g18,g19)
    c: InternalAlignment(g20,g19)
    c: InternalAlignment(g21,g19)
    c: Weight(g22) = 1
    c: Equal(g22,g23)
    c: Equal(g22,g24)
    c: InternalAlignment(g22,g25)
    c: InternalAlignment(g23,g25)
    c: InternalAlignment(g24,g25)
    c: InternalAlignment(g26,g25)
    c: InternalAlignment(g27,g25)
    c: Block(g25)
    c: Block(g19)
    c: Weight(g28) = 1
    c: Equal(g28,g29)
    c: Equal(g28,g30)
    c: InternalAlignment(g28,g31)
    c: InternalAlignment(g29,g31)
    c: InternalAlignment(g30,g31)
    c: InternalAlignment(g32,g31)
    c: InternalAlignment(g33,g31)
    c: Weight(g34) = 1
    c: Equal(g34,g35)
    c: Equal(g34,g36)
    c: InternalAlignment(g34,g37)
    c: InternalAlignment(g35,g37)
    c: InternalAlignment(g36,g37)
    c: InternalAlignment(g38,g37)
    c: InternalAlignment(g39,g37)
    c: Block(g37)
    c: Block(g31)
    c: Weight(g40) = 1
    c: Equal(g40,g41)
    c: Equal(g40,g42)
    c: InternalAlignment(g40,g43)
    c: InternalAlignment(g41,g43)
    c: InternalAlignment(g42,g43)
    c: InternalAlignment(g44,g43)
    c: InternalAlignment(g45,g43)
    c: Weight(g46) = 1
    c: Equal(g46,g47)
    c: Equal(g46,g48)
    c: InternalAlignment(g46,g49)
    c: InternalAlignment(g47,g49)
    c: InternalAlignment(g48,g49)
    c: InternalAlignment(g50,g49)
    c: InternalAlignment(g51,g49)
    c: Block(g43)
    c: Block(g49)
    c: Coincident(g52,g7)
    c: Coincident(g52,g6)
    c: Horizontal(g52)
    c: Distance(g52) = 450
    c: Coincident(g53,g7)
    c: Coincident(g53,g6)
    c: Horizontal(g53)
    c: Horizontal(g54)
    c: Coincident(g5,g54)
    c: Horizontal(g55)
    c: Vertical(g56)
    c: Block(g56)
    c: Block(g55)
    c: Block(g54)
    c: Distance(g56) = 18.3554
    c: Coincident(g58,g56)
    c: Coincident(g58,g57)
    c: Horizontal(g58)
    c: Block(g58)
    c: Block(g57)
    c: Coincident(g55,g57)
    c: Coincident(g1,g54)
    c: Weight(g59) = 1
    c: Equal(g59,g60)
    c: Equal(g59,g61)
    c: InternalAlignment(g59,g62)
    c: InternalAlignment(g60,g62)
    c: InternalAlignment(g61,g62)
    c: InternalAlignment(g63,g62)
    c: InternalAlignment(g64,g62)
    c: Block(g62)
    c: Weight(g65) = 1
    c: Equal(g65,g66)
    c: Equal(g65,g67)
    c: InternalAlignment(g65,g68)
    c: InternalAlignment(g66,g68)
    c: InternalAlignment(g67,g68)
    c: InternalAlignment(g69,g68)
    c: InternalAlignment(g70,g68)
    c: Block(g68)
    c: Weight(g71) = 1
    c: Equal(g71,g72)
    c: Equal(g71,g73)
    c: InternalAlignment(g71,g74)
    c: InternalAlignment(g72,g74)
    c: InternalAlignment(g73,g74)
    c: InternalAlignment(g75,g74)
    c: InternalAlignment(g76,g74)
    c: Block(g74)
    c: Weight(g77) = 1
    c: Equal(g77,g78)
    c: Equal(g77,g79)
    c: InternalAlignment(g77,g80)
    c: InternalAlignment(g78,g80)
    c: InternalAlignment(g79,g80)
    c: InternalAlignment(g81,g80)
    c: InternalAlignment(g82,g80)
    c: Block(g80)
    c: Weight(g83) = 1
    c: Equal(g83,g84)
    c: Equal(g83,g85)
    c: InternalAlignment(g83,g86)
    c: InternalAlignment(g84,g86)
    c: InternalAlignment(g85,g86)
    c: InternalAlignment(g87,g86)
    c: InternalAlignment(g88,g86)
    c: Weight(g89) = 1
    c: Equal(g89,g90)
    c: Equal(g89,g91)
    c: InternalAlignment(g89,g92)
    c: InternalAlignment(g90,g92)
    c: InternalAlignment(g91,g92)
    c: InternalAlignment(g93,g92)
    c: InternalAlignment(g94,g92)
    c: Block(g86)
    c: Block(g92)
    c: Coincident(g95,g86)
    c: Coincident(g95,g92)
    c: Vertical(g95)
    c: Coincident(g96,g86)
    c: Coincident(g96,g68)
    c: Coincident(g97,g68)
    c: Coincident(g97,g92)
    c: Weight(g98) = 1
    c: Equal(g98,g99)
    c: Equal(g98,g100)
    c: InternalAlignment(g98,g101)
    c: InternalAlignment(g99,g101)
    c: InternalAlignment(g100,g101)
    c: InternalAlignment(g102,g101)
    c: InternalAlignment(g103,g101)
    c: Weight(g104) = 1
    c: Equal(g104,g105)
    c: Equal(g104,g106)
    c: InternalAlignment(g104,g107)
    c: InternalAlignment(g105,g107)
    c: InternalAlignment(g106,g107)
    c: InternalAlignment(g108,g107)
    c: InternalAlignment(g109,g107)
    c: Block(g101)
    c: Block(g107)
    c: Coincident(g110,g101)
    c: Coincident(g110,g107)
    c: Vertical(g110)
    c: Coincident(g111,g101)
    c: Coincident(g111,g62)
    c: Coincident(g112,g62)
    c: Coincident(g112,g107)
    c: Weight(g113) = 1
    c: Equal(g113,g114)
    c: Equal(g113,g115)
    c: InternalAlignment(g113,g116)
    c: InternalAlignment(g114,g116)
    c: InternalAlignment(g115,g116)
    c: InternalAlignment(g117,g116)
    c: InternalAlignment(g118,g116)
    c: Weight(g119) = 1
    c: Equal(g119,g120)
    c: Equal(g119,g121)
    c: InternalAlignment(g119,g122)
    c: InternalAlignment(g120,g122)
    c: InternalAlignment(g121,g122)
    c: InternalAlignment(g123,g122)
    c: InternalAlignment(g124,g122)
    c: Block(g116)
    c: Block(g122)
    c: Coincident(g125,g116)
    c: Coincident(g125,g122)
    c: Vertical(g125)
    c: Coincident(g126,g122)
    c: Coincident(g126,g80)
    c: Coincident(g127,g80)
    c: Coincident(g127,g116)
    c: Weight(g128) = 1
    c: Equal(g128,g129)
    c: Equal(g128,g130)
    c: InternalAlignment(g128,g131)
    c: InternalAlignment(g129,g131)
    c: InternalAlignment(g130,g131)
    c: InternalAlignment(g132,g131)
    c: InternalAlignment(g133,g131)
    c: Weight(g134) = 1
    c: Equal(g134,g135)
    c: Equal(g134,g136)
    c: InternalAlignment(g134,g137)
    c: InternalAlignment(g135,g137)
    c: InternalAlignment(g136,g137)
    c: InternalAlignment(g138,g137)
    c: InternalAlignment(g139,g137)
    c: Block(g131)
    c: Block(g137)
    c: Coincident(g140,g131)
    c: Coincident(g140,g137)
    c: Vertical(g140)
    c: Coincident(g141,g137)
    c: Coincident(g141,g74)
    c: Coincident(g142,g74)
    c: Coincident(g142,g131)
    c: Weight(g143) = 1
    c: Equal(g143,g144)
    c: Equal(g143,g145)
    c: InternalAlignment(g143,g146)
    c: InternalAlignment(g144,g146)
    c: InternalAlignment(g145,g146)
    c: InternalAlignment(g147,g146)
    c: InternalAlignment(g148,g146)
    c: Weight(g149) = 1
    c: Equal(g149,g150)
    c: Equal(g149,g151)
    c: InternalAlignment(g149,g152)
    c: InternalAlignment(g150,g152)
    c: InternalAlignment(g151,g152)
    c: InternalAlignment(g153,g152)
    c: InternalAlignment(g154,g152)
    c: Weight(g155) = 1
    c: Equal(g155,g156)
    c: Equal(g155,g157)
    c: InternalAlignment(g155,g158)
    c: InternalAlignment(g156,g158)
    c: InternalAlignment(g157,g158)
    c: InternalAlignment(g159,g158)
    c: InternalAlignment(g160,g158)
    c: Weight(g161) = 1
    c: Equal(g161,g162)
    c: Equal(g161,g163)
    c: InternalAlignment(g161,g164)
    c: InternalAlignment(g162,g164)
    c: InternalAlignment(g163,g164)
    c: InternalAlignment(g165,g164)
    c: InternalAlignment(g166,g164)
    c: Block(g164)
    c: Block(g158)
    c: Block(g152)
    c: Block(g146)
    c: Coincident(g167,g37)
    c: Coincident(g167,g164)
    c: Coincident(g168,g164)
    c: Coincident(g168,g158)
    c: Horizontal(g168)
    c: Coincident(g169,g158)
    c: Coincident(g169,g37)
    c: Vertical(g169)
    c: Coincident(g170,g31)
    c: Coincident(g170,g152)
    c: Vertical(g170)
    c: Coincident(g171,g152)
    c: Coincident(g171,g146)
    c: Horizontal(g171)
    c: Coincident(g172,g146)
    c: Coincident(g172,g31)
    c: Weight(g173) = 1
    c: Equal(g173,g174)
    c: Equal(g173,g175)
    c: InternalAlignment(g173,g176)
    c: InternalAlignment(g174,g176)
    c: InternalAlignment(g175,g176)
    c: InternalAlignment(g177,g176)
    c: InternalAlignment(g178,g176)
    c: Weight(g179) = 1
    c: Equal(g179,g180)
    c: Equal(g179,g181)
    c: InternalAlignment(g179,g182)
    c: InternalAlignment(g180,g182)
    c: InternalAlignment(g181,g182)
    c: InternalAlignment(g183,g182)
    c: InternalAlignment(g184,g182)
    c: Weight(g185) = 1
    c: Equal(g185,g186)
    c: Equal(g185,g187)
    c: InternalAlignment(g185,g188)
    c: InternalAlignment(g186,g188)
    c: InternalAlignment(g187,g188)
    c: InternalAlignment(g189,g188)
    c: InternalAlignment(g190,g188)
    c: Weight(g191) = 1
    c: Equal(g191,g192)
    c: Equal(g191,g193)
    c: InternalAlignment(g191,g194)
    c: InternalAlignment(g192,g194)
    c: InternalAlignment(g193,g194)
    c: InternalAlignment(g195,g194)
    c: InternalAlignment(g196,g194)
    c: Block(g194)
    c: Block(g188)
    c: Block(g182)
    c: Block(g176)
    c: Coincident(g197,g194)
    c: Coincident(g197,g188)
    c: Horizontal(g197)
    c: Coincident(g198,g188)
    c: Coincident(g198,g19)
    c: Vertical(g198)
    c: Coincident(g199,g25)
    c: Coincident(g199,g182)
    c: Vertical(g199)
    c: Coincident(g200,g182)
    c: Coincident(g200,g176)
    c: Horizontal(g200)
    c: Coincident(g201,g176)
    c: Coincident(g201,g25)
    c: Coincident(g202,g19)
    c: Weight(g203) = 1
    c: Equal(g203,g204)
    c: Equal(g203,g205)
    c: InternalAlignment(g203,g206)
    c: InternalAlignment(g204,g206)
    c: InternalAlignment(g205,g206)
    c: InternalAlignment(g207,g206)
    c: InternalAlignment(g208,g206)
    c: Weight(g209) = 1
    c: Equal(g209,g210)
    c: Equal(g209,g211)
    c: InternalAlignment(g209,g212)
    c: InternalAlignment(g210,g212)
    c: InternalAlignment(g211,g212)
    c: InternalAlignment(g213,g212)
    c: InternalAlignment(g214,g212)
    c: Block(g212)
    c: Block(g206)
    c: Coincident(g215,g212)
    c: Coincident(g215,g43)
    c: Coincident(g216,g43)
    c: Coincident(g216,g206)
    c: Coincident(g217,g206)
    c: Coincident(g217,g212)
    c: Vertical(g217)
    c: Weight(g218) = 1
    c: Equal(g218,g219)
    c: Equal(g218,g220)
    c: InternalAlignment(g218,g221)
    c: InternalAlignment(g219,g221)
    c: InternalAlignment(g220,g221)
    c: InternalAlignment(g222,g221)
    c: InternalAlignment(g223,g221)
    c: Weight(g224) = 1
    c: Equal(g224,g225)
    c: Equal(g224,g226)
    c: InternalAlignment(g224,g227)
    c: InternalAlignment(g225,g227)
    c: InternalAlignment(g226,g227)
    c: InternalAlignment(g228,g227)
    c: InternalAlignment(g229,g227)
    c: Block(g227)
    c: Block(g221)
    c: Coincident(g230,g221)
    c: Coincident(g230,g49)
    c: Coincident(g231,g49)
    c: Coincident(g231,g227)
    c: Coincident(g232,g227)
    c: Coincident(g232,g221)
    c: Vertical(g232)
    c: Horizontal(g233)
    c: Block(g233)
    c: Vertical(g234)
    c: Block(g234)
    c: Block(g235)
    c: Weight(g236) = 1
    c: Equal(g236,g237)
    c: Equal(g236,g238)
    c: InternalAlignment(g236,g239)
    c: InternalAlignment(g237,g239)
    c: InternalAlignment(g238,g239)
    c: InternalAlignment(g240,g239)
    c: InternalAlignment(g241,g239)
    c: Weight(g242) = 1
    c: Equal(g242,g243)
    c: Equal(g242,g244)
    c: InternalAlignment(g242,g245)
    c: InternalAlignment(g243,g245)
    c: InternalAlignment(g244,g245)
    c: InternalAlignment(g246,g245)
    c: InternalAlignment(g247,g245)
    c: Weight(g248) = 1
    c: Equal(g248,g249)
    c: Equal(g248,g250)
    c: InternalAlignment(g248,g251)
    c: InternalAlignment(g249,g251)
    c: InternalAlignment(g250,g251)
    c: InternalAlignment(g252,g251)
    c: InternalAlignment(g253,g251)
    c: Weight(g254) = 1
    c: Equal(g254,g255)
    c: Equal(g254,g256)
    c: InternalAlignment(g254,g257)
    c: InternalAlignment(g255,g257)
    c: InternalAlignment(g256,g257)
    c: InternalAlignment(g258,g257)
    c: InternalAlignment(g259,g257)
    c: Block(g239)
    c: Block(g245)
    c: Block(g251)
    c: Block(g257)
    c: Coincident(g260,g245)
    c: Coincident(g260,g239)
    c: Horizontal(g260)
    c: Block(g202)
    c: Weight(g261) = 1
    c: Equal(g261,g262)
    c: Equal(g261,g263)
    c: InternalAlignment(g261,g264)
    c: InternalAlignment(g262,g264)
    c: InternalAlignment(g263,g264)
    c: InternalAlignment(g265,g264)
    c: InternalAlignment(g266,g264)
    c: Weight(g267) = 1
    c: Equal(g267,g268)
    c: Equal(g267,g269)
    c: InternalAlignment(g267,g270)
    c: InternalAlignment(g268,g270)
    c: InternalAlignment(g269,g270)
    c: InternalAlignment(g271,g270)
    c: InternalAlignment(g272,g270)
    c: Weight(g273) = 1
    c: Equal(g273,g274)
    c: Equal(g273,g275)
    c: InternalAlignment(g273,g276)
    c: InternalAlignment(g274,g276)
    c: InternalAlignment(g275,g276)
    c: InternalAlignment(g277,g276)
    c: InternalAlignment(g278,g276)
    c: Weight(g279) = 1
    c: Equal(g279,g280)
    c: Equal(g279,g281)
    c: InternalAlignment(g279,g282)
    c: InternalAlignment(g280,g282)
    c: InternalAlignment(g281,g282)
    c: InternalAlignment(g283,g282)
    c: InternalAlignment(g284,g282)
    c: Block(g264)
    c: Block(g270)
    c: Block(g276)
    c: Block(g282)
    c: Coincident(g285,g276)
    c: Coincident(g285,g282)
    c: Horizontal(g285)
    c: Coincident(g286,g282)
    c: Coincident(g286,g264)
    c: Vertical(g286)
    c: Coincident(g287,g264)
    c: Coincident(g287,g270)
    c: Coincident(g288,g270)
    c: Coincident(g288,g276)
    c: Vertical(g288)
    c: Weight(g289) = 1
    c: Equal(g289,g290)
    c: Equal(g289,g291)
    c: InternalAlignment(g289,g292)
    c: InternalAlignment(g290,g292)
    c: InternalAlignment(g291,g292)
    c: InternalAlignment(g293,g292)
    c: InternalAlignment(g294,g292)
    c: Weight(g295) = 1
    c: Equal(g295,g296)
    c: Equal(g295,g297)
    c: InternalAlignment(g295,g298)
    c: InternalAlignment(g296,g298)
    c: InternalAlignment(g297,g298)
    c: InternalAlignment(g299,g298)
    c: InternalAlignment(g300,g298)
    c: Weight(g301) = 1
    c: Equal(g301,g302)
    c: Equal(g301,g303)
    c: InternalAlignment(g301,g304)
    c: InternalAlignment(g302,g304)
    c: InternalAlignment(g303,g304)
    c: InternalAlignment(g305,g304)
    c: InternalAlignment(g306,g304)
    c: Block(g304)
    c: Block(g298)
    c: Block(g292)
    c: Coincident(g307,g298)
    c: Coincident(g307,g292)
    c: Coincident(g308,g292)
    c: Coincident(g308,g304)
    c: Vertical(g308)
    c: Coincident(g309,g304)
    c: Coincident(g309,g298)
    c: Horizontal(g309)
    c: Horizontal(g310)
    c: Horizontal(g313)
    c: Horizontal(g314)
    c: Vertical(g315)
    c: Vertical(g316)
    c: Horizontal(g317)
    c: Distance(g316) = 4
    c: Distance(g317) = 4
    c: Distance(g315) = 4
    c: Distance(g314) = 4
    c: Distance(g313) = 4
    c: Distance(g312) = 4
    c: Distance(g311) = 4
    c: Distance(g310) = 4
    c: Parallel(g57,g311)
    c: Parallel(g57,g312)
    c: Coincident(g312,g55)
    c: Coincident(g313,g55)
    c: Coincident(g314,g315)
    c: Coincident(g314,g55)
    c: Coincident(g316,g317)
    c: Coincident(g56,g316)
    c: Coincident(g310,g311)
    c: Coincident(g310,g57)
FEATURE [Sketcher::SketchObject] Sketch001
  FullyConstrained = true
  MapMode = 4
  Placement = pos=(0,0,0) rot=(0.57735,0.57735,0.57735;2.0944rad)
  Support = -> [Sketch]
  sketch-geometry (46):
    g0: BSplineCurve PolesCount=3 KnotsCount=2 Degree=2 IsPeriodic=0
    g1: ArcOfCircle CenterX=73.1223 CenterY=-32.291 CenterZ=0 NormalX=0 NormalY=0 NormalZ=1 AngleXU=0 Radius=13 StartAngle=5.92268 EndAngle=9.06428
    g2: ArcOfCircle CenterX=66.7816 CenterY=-49.1439 CenterZ=0 NormalX=0 NormalY=0 NormalZ=1 AngleXU=0 Radius=13 StartAngle=2.78068 EndAngle=5.92131
    g3: ArcOfCircle CenterX=55.9263 CenterY=-78.1807 CenterZ=0 NormalX=0 NormalY=0 NormalZ=1 AngleXU=0 Radius=13 StartAngle=5.92268 EndAngle=9.06428
    g4: ArcOfCircle CenterX=49.5884 CenterY=-95.0342 CenterZ=0 NormalX=0 NormalY=0 NormalZ=1 AngleXU=0 Radius=13 StartAngle=2.78068 EndAngle=5.92131
    g5: ArcOfCircle CenterX=38.7206 CenterY=-124.067 CenterZ=0 NormalX=0 NormalY=0 NormalZ=1 AngleXU=0 Radius=13 StartAngle=5.92268 EndAngle=9.06428
    g6: ArcOfCircle CenterX=32.3875 CenterY=-140.92 CenterZ=0 NormalX=0 NormalY=0 NormalZ=1 AngleXU=0 Radius=13 StartAngle=2.78068 EndAngle=5.92131
    g7: ArcOfCircle CenterX=21.4715 CenterY=-169.934 CenterZ=0 NormalX=0 NormalY=0 NormalZ=1 AngleXU=0 Radius=13 StartAngle=5.92268 EndAngle=9.06428
    g8: ArcOfCircle CenterX=15.1336 CenterY=-186.787 CenterZ=0 NormalX=0 NormalY=0 NormalZ=1 AngleXU=0 Radius=13 StartAngle=2.78068 EndAngle=5.92131
    g9-g12: Circle x4 (B-spline internal-alignment scaffolding for g13; pole/knot coordinates omitted)
    g13: BSplineCurve PolesCount=4 KnotsCount=2 Degree=3 IsPeriodic=0
    g14: GeomPoint X=28.8094 Y=-19.0875 Z=0
    g15: GeomPoint X=47.0443 Y=-50.4712 Z=0
    g16: Circle CenterX=53.5586 CenterY=-23.2695 CenterZ=0 NormalX=0 NormalY=0 NormalZ=1 AngleXU=0 Radius=3.24518
    g17: Circle CenterX=-13.2144 CenterY=-179.544 CenterZ=0 NormalX=0 NormalY=0 NormalZ=1 AngleXU=0 Radius=9.75982
    g18: Circle CenterX=0.933922 CenterY=-166.43 CenterZ=0 NormalX=0 NormalY=0 NormalZ=1 AngleXU=0 Radius=3.0096
    g19: Circle CenterX=-33.9842 CenterY=-177.188 CenterZ=0 NormalX=0 NormalY=0 NormalZ=1 AngleXU=0 Radius=4.6873
    g20: Circle CenterX=-47.512 CenterY=-174.517 CenterZ=0 NormalX=0 NormalY=0 NormalZ=1 AngleXU=0 Radius=2.4311
    g21: Circle CenterX=-56.5538 CenterY=-172.165 CenterZ=0 NormalX=0 NormalY=0 NormalZ=1 AngleXU=0 Radius=1.39683
    g22: ArcOfCircle CenterX=51.2151 CenterY=-198.473 CenterZ=0 NormalX=0 NormalY=0 NormalZ=1 AngleXU=0 Radius=20 StartAngle=2.78189 EndAngle=4.35269
    g23: LineSegment StartX=32.4951 StartY=-191.433 StartZ=0 EndX=94.6578 EndY=-26.1352 EndZ=0
    g24: LineSegment StartX=43.1192 StartY=-220.001 StartZ=0 EndX=44.1752 EndY=-217.193 EndZ=0
    g25: LineSegment StartX=117.223 StartY=-19.0875 StartZ=0 EndX=117.223 EndY=-16.0875 EndZ=0
    g26: LineSegment StartX=117.223 StartY=-16.0875 StartZ=0 EndX=17.2232 EndY=-16.0875 EndZ=0
    g27: LineSegment StartX=17.2232 StartY=-16.0875 StartZ=0 EndX=17.2232 EndY=-19.0875 EndZ=0
    g28: LineSegment StartX=28.8094 StartY=-19.0875 StartZ=0 EndX=17.2232 EndY=-19.0875 EndZ=0
    g29: LineSegment StartX=85.2866 StartY=-36.8766 StartZ=0 EndX=78.9396 EndY=-53.7463 EndZ=0
    g30: LineSegment StartX=60.9579 StartY=-27.7053 StartZ=0 EndX=54.6191 EndY=-44.5532 EndZ=0
    g31: LineSegment StartX=68.0907 StartY=-82.7664 StartZ=0 EndX=61.7465 EndY=-99.6365 EndZ=0
    g32: LineSegment StartX=43.7619 StartY=-73.595 StartZ=0 EndX=37.426 EndY=-90.4435 EndZ=0
    g33: LineSegment StartX=50.885 StartY=-128.652 StartZ=0 EndX=44.5456 EndY=-145.522 EndZ=0
    g34: LineSegment StartX=26.5562 StartY=-119.481 StartZ=0 EndX=20.2251 EndY=-136.329 EndZ=0
    g35: LineSegment StartX=9.3071 StartY=-165.349 StartZ=0 EndX=2.97115 EndY=-182.197 EndZ=0
    g36: LineSegment StartX=33.6358 StartY=-174.52 StartZ=0 EndX=27.2917 EndY=-191.39 EndZ=0
    g37: LineSegment StartX=43.1192 StartY=-220.001 StartZ=0 EndX=-173.309 EndY=-142.162 EndZ=0
    g38: LineSegment StartX=-173.309 StartY=-142.162 StartZ=0 EndX=-172.294 EndY=-139.339 EndZ=0
    g39: Circle CenterX=12.8789 CenterY=-141.321 CenterZ=0 NormalX=0 NormalY=0 NormalZ=1 AngleXU=0 Radius=1
    g40: Circle CenterX=-8.22352 CenterY=-197.285 CenterZ=0 NormalX=0 NormalY=0 NormalZ=1 AngleXU=0 Radius=1
    g41: Circle CenterX=-172.294 CenterY=-139.339 CenterZ=0 NormalX=0 NormalY=0 NormalZ=1 AngleXU=0 Radius=1
    g42: BSplineCurve PolesCount=3 KnotsCount=2 Degree=2 IsPeriodic=0
    g43: GeomPoint X=12.8789 Y=-141.321 Z=0
    g44: GeomPoint X=-172.294 Y=-139.339 Z=0
    g45: LineSegment StartX=12.8789 StartY=-141.321 StartZ=0 EndX=47.0443 EndY=-50.4712 EndZ=0
  constraints (74):
    c: Block(g0)
    c: Block(g1)
    c: Block(g2)
    c: Block(g4)
    c: Block(g3)
    c: Block(g6)
    c: Block(g5)
    c: Block(g8)
    c: Block(g7)
    c: Weight(g9) = 1
    c: Equal(g9,g10)
    c: Equal(g9,g11)
    c: Equal(g9,g12)
    c: InternalAlignment(g9-g12 -> g13) x4
    c: InternalAlignment(g14,g13)
    c: InternalAlignment(g15,g13)
    c: Block(g16)
    c: Block(g22)
    c: Coincident(g23,g22)
    c: Coincident(g23,g0)
    c: Block(g13)
    c: Coincident(g24,g22)
    c: Block(g24)
    c: Coincident(g25,g0)
    c: Vertical(g25)
    c: Coincident(g26,g25)
    c: Horizontal(g26)
    c: Coincident(g27,g26)
    c: Vertical(g27)
    c: Block(g26)
    c: Coincident(g28,g13)
    c: Coincident(g28,g27)
    c: Horizontal(g28)
    c: Coincident(g29,g1)
    c: Coincident(g29,g2)
    c: Coincident(g30,g1)
    c: Coincident(g30,g2)
    c: Coincident(g31,g3)
    c: Coincident(g31,g4)
    c: Coincident(g32,g3)
    c: Coincident(g32,g4)
    c: Coincident(g33,g5)
    c: Coincident(g33,g6)
    c: Coincident(g34,g5)
    c: Coincident(g34,g6)
    c: Coincident(g35,g7)
    c: Coincident(g35,g8)
    c: Coincident(g36,g7)
    c: Coincident(g36,g8)
    c: Distance(g26) = 100
    c: Distance(g37) = 230
    c: Coincident(g37,g24)
    c: Perpendicular(g38,g37)
    c: Distance(g38) = 3
    c: Block(g37)
    c: Coincident(g38,g37)
    c: Weight(g39) = 1
    c: Equal(g39,g40)
    c: Equal(g39,g41)
    c: Coincident(g42,g38)
    c: InternalAlignment(g39,g42)
    c: InternalAlignment(g40,g42)
    c: InternalAlignment(g41,g42)
    c: InternalAlignment(g43,g42)
    c: InternalAlignment(g44,g42)
    c: Coincident(g45,g42)
    c: Coincident(g45,g13)
    c: Block(g45)
    c: Block(g42)
    c: Block(g18)
    c: Block(g17)
    c: Block(g19)
    c: Block(g20)
    c: Block(g21)
FEATURE [Part::Extrusion] Extrude002
  Base = -> Sketch001
  Dir = (1,0,0)
  DirMode = 2
  FaceMakerClass = Part::FaceMakerBullseye
  LengthFwd = 8
  LengthRev = 0
  Solid = true
  Symmetric = false
FEATURE [Sketcher::SketchObject] Sketch002
  FullyConstrained = true
  sketch-geometry (20):
    g0: LineSegment StartX=-2.77179 StartY=-200.304 StartZ=0 EndX=5.22821 EndY=-200.304 EndZ=0
    g1: LineSegment StartX=5.22821 StartY=-200.304 StartZ=0 EndX=5.22821 EndY=-197.304 EndZ=0
    g2: LineSegment StartX=-2.77179 StartY=-200.304 StartZ=0 EndX=-2.77179 EndY=-197.304 EndZ=0
    g3: LineSegment StartX=5.22821 StartY=-197.304 StartZ=0 EndX=8.22821 EndY=-197.304 EndZ=0
    g4: LineSegment StartX=-2.77179 StartY=-197.304 StartZ=0 EndX=-5.77179 EndY=-197.304 EndZ=0
    g5: LineSegment StartX=19.2282 StartY=-203.304 StartZ=0 EndX=19.2282 EndY=-206.304 EndZ=0
    g6: LineSegment StartX=-16.7718 StartY=-203.304 StartZ=0 EndX=-16.7718 EndY=-206.304 EndZ=0
    g7: LineSegment StartX=-16.7718 StartY=-206.304 StartZ=0 EndX=19.2282 EndY=-206.304 EndZ=0
    g8: Circle CenterX=-16.7718 CenterY=-203.304 CenterZ=0 NormalX=0 NormalY=0 NormalZ=1 AngleXU=0 Radius=1
    g9: Circle CenterX=-5.77179 CenterY=-203.304 CenterZ=0 NormalX=0 NormalY=0 NormalZ=1 AngleXU=0 Radius=1
    g10: Circle CenterX=-5.77179 CenterY=-197.304 CenterZ=0 NormalX=0 NormalY=0 NormalZ=1 AngleXU=0 Radius=1
    g11: BSplineCurve PolesCount=3 KnotsCount=2 Degree=2 IsPeriodic=0
    g12: GeomPoint X=-16.7718 Y=-203.304 Z=0
    g13: GeomPoint X=-5.77179 Y=-197.304 Z=0
    g14: Circle CenterX=19.2282 CenterY=-203.304 CenterZ=0 NormalX=0 NormalY=0 NormalZ=1 AngleXU=0 Radius=1
    g15: Circle CenterX=8.22821 CenterY=-203.304 CenterZ=0 NormalX=0 NormalY=0 NormalZ=1 AngleXU=0 Radius=1
    g16: Circle CenterX=8.22821 CenterY=-197.304 CenterZ=0 NormalX=0 NormalY=0 NormalZ=1 AngleXU=0 Radius=1
    g17: BSplineCurve PolesCount=3 KnotsCount=2 Degree=2 IsPeriodic=0
    g18: GeomPoint X=19.2282 Y=-203.304 Z=0
    g19: GeomPoint X=8.22821 Y=-197.304 Z=0
  constraints (41):
    c: Horizontal(g0)
    c: Distance(g0) = 8
    c: Coincident(g1,g0)
    c: Vertical(g1)
    c: Distance(g1) = 3
    c: Coincident(g2,g0)
    c: Vertical(g2)
    c: Distance(g2) = 3
    c: Coincident(g3,g1)
    c: Horizontal(g3)
    c: Distance(g3) = 3
    c: Coincident(g4,g2)
    c: Horizontal(g4)
    c: Distance(g4) = 3
    c: Vertical(g5)
    c: Vertical(g6)
    c: Coincident(g7,g6)
    c: Coincident(g7,g5)
    c: Weight(g8) = 1
    c: Equal(g8,g9)
    c: Equal(g8,g10)
    c: Coincident(g11,g4)
    c: InternalAlignment(g8,g11)
    c: InternalAlignment(g9,g11)
    c: InternalAlignment(g10,g11)
    c: InternalAlignment(g12,g11)
    c: InternalAlignment(g13,g11)
    c: Coincident(g17,g5)
    c: Weight(g14) = 1
    c: Equal(g14,g15)
    c: Equal(g14,g16)
    c: Coincident(g17,g3)
    c: InternalAlignment(g14,g17)
    c: InternalAlignment(g15,g17)
    c: InternalAlignment(g16,g17)
    c: InternalAlignment(g18,g17)
    c: InternalAlignment(g19,g17)
    c: Block(g7)
    c: Block(g17)
    c: Block(g11)
    c: Block(g6)
FEATURE [Part::Extrusion] Extrude003
  Base = -> Sketch002
  Dir = (0,0,1)
  DirMode = 2
  FaceMakerClass = Part::FaceMakerBullseye
  LengthFwd = 260
  LengthRev = 0
  Solid = true
  Symmetric = false
FEATURE [Part::Extrusion] Extrude
  Base = -> Sketch
  Dir = (0,0,1)
  DirMode = 2
  FaceMakerClass = Part::FaceMakerBullseye
  LengthFwd = 14
  LengthRev = 0
  Solid = true
  Symmetric = false
